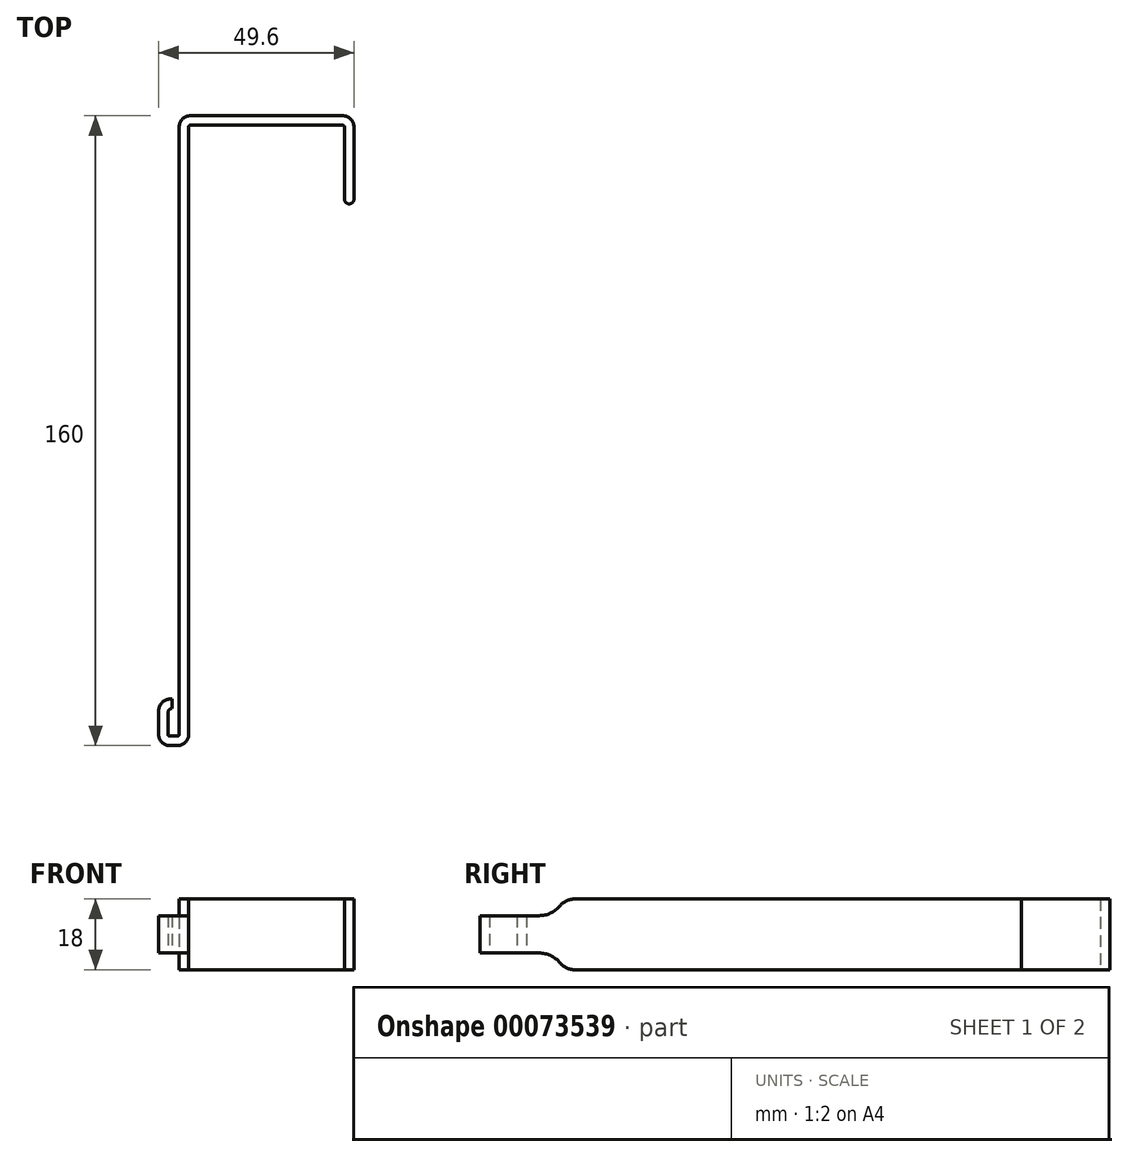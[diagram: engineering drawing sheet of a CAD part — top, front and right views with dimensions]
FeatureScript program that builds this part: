
annotation { "Feature Type Name" : "Feature", "Feature Type Description" : "" }
export const myFeature = defineFeature(function(context is Context, id is Id, definition is map)
    precondition{}
    {
        {
            var Q0;
            Q0=qCreatedBy(makeId("Top.planeOp"),FACE);
            var sketch = newSketch(context, id + "F0", { "sketchPlane" : qUnion([Q0])});
            skLineSegment(sketch, "E0", {"start": v(44.4, -21.2) * mm, "end": v(44.4, -2.9) * mm});
            skLineSegment(sketch, "E1", {"start": v(41.5, 0) * mm, "end": v(2.9, 0) * mm});
            skLineSegment(sketch, "E2", {"start": v(0, -2.9) * mm, "end": v(0, -157.3) * mm});
            skLineSegment(sketch, "E3", {"start": v(2.4, -157.3) * mm, "end": v(2.4, -2.9) * mm});
            skLineSegment(sketch, "E4", {"start": v(2.9, -2.4) * mm, "end": v(41.5, -2.4) * mm});
            skLineSegment(sketch, "E5", {"start": v(42, -2.9) * mm, "end": v(42, -21.2) * mm});
            skArc(sketch, "E6", {"start": v(42, -21.2) * mm, "mid": v(43.2, -22.4) * mm, "end": v(44.4, -21.2) * mm});
            skPoint(sketch, "E7.visualSharp", {"position": v(2.4, -2.4) * mm});
            skArc(sketch, "E7.filletArc", {"start": v(2.9, -2.4) * mm, "mid": v(2.55, -2.55) * mm, "end": v(2.4, -2.9) * mm});
            skPoint(sketch, "E8.visualSharp", {"position": v(42, -2.4) * mm});
            skArc(sketch, "E8.filletArc", {"start": v(42, -2.9) * mm, "mid": v(41.85, -2.55) * mm, "end": v(41.5, -2.4) * mm});
            skPoint(sketch, "E9.visualSharp", {"position": v(44.4, 0) * mm});
            skArc(sketch, "E9.filletArc", {"start": v(44.4, -2.9) * mm, "mid": v(43.55, -0.85) * mm, "end": v(41.5, 0) * mm});
            skPoint(sketch, "E10.visualSharp", {"position": v(0, 0) * mm});
            skArc(sketch, "E10.filletArc", {"start": v(2.9, 0) * mm, "mid": v(0.85, -0.85) * mm, "end": v(0, -2.9) * mm});
            skLineSegment(sketch, "E11", {"start": v(-0.3, -160) * mm, "end": v(-2.5, -160) * mm});
            skLineSegment(sketch, "E12", {"start": v(-5.2, -157.3) * mm, "end": v(-5.2, -151.2) * mm});
            skLineSegment(sketch, "E13", {"start": v(-2.2, -148.2) * mm, "end": v(-1.8, -148.2) * mm});
            skLineSegment(sketch, "E14", {"start": v(-1.8, -148.2) * mm, "end": v(-1.8, -150.6) * mm});
            skLineSegment(sketch, "E15", {"start": v(-2.8, -151.6) * mm, "end": v(-2.8, -157.3) * mm});
            skLineSegment(sketch, "E16", {"start": v(-2.5, -157.6) * mm, "end": v(-0.3, -157.6) * mm});
            skPoint(sketch, "E17.visualSharp", {"position": v(-2.8, -157.6) * mm});
            skArc(sketch, "E17.filletArc", {"start": v(-2.8, -157.3) * mm, "mid": v(-2.71, -157.51) * mm, "end": v(-2.5, -157.6) * mm});
            skPoint(sketch, "E18.visualSharp", {"position": v(0, -157.6) * mm});
            skArc(sketch, "E18.filletArc", {"start": v(-0.3, -157.6) * mm, "mid": v(-0.09, -157.51) * mm, "end": v(0, -157.3) * mm});
            skPoint(sketch, "E19.visualSharp", {"position": v(2.4, -160) * mm});
            skArc(sketch, "E19.filletArc", {"start": v(-0.3, -160) * mm, "mid": v(1.6, -159.2) * mm, "end": v(2.4, -157.3) * mm});
            skPoint(sketch, "E20.visualSharp", {"position": v(-5.2, -160) * mm});
            skArc(sketch, "E20.filletArc", {"start": v(-5.2, -157.3) * mm, "mid": v(-4.4, -159.2) * mm, "end": v(-2.5, -160) * mm});
            skArc(sketch, "E21.filletArc", {"start": v(-1.8, -150.6) * mm, "mid": v(-2.5, -150.9) * mm, "end": v(-2.8, -151.6) * mm});
            skArc(sketch, "E22.filletArc", {"start": v(-2.2, -148.2) * mm, "mid": v(-4.32, -149.08) * mm, "end": v(-5.2, -151.2) * mm});
            skSolve(sketch);
        }
        {
            var Q0;
            Q0=makeQuery(id+"F0.imprint","IMPRINT",FACE,{"disambiguationData":[TD([[makeQuery(id+"F0.imprint","IMPRINT",EDGE,{"derivedFrom":sQuery(id+"F0.wireOp",EDGE,"E0")}),1.0]])]});
            extrude(context, id + "F1", {"entities" : qUnion([Q0]), "depth" : 18 * mm, "symmetric" : true});
        }
        {
            var Q0;
            Q0=qCreatedBy(makeId("Right.planeOp"),FACE);
            var sketch = newSketch(context, id + "F2", { "sketchPlane" : qUnion([Q0])});
            skArc(sketch, "E23", {"start": v(-145, 4.75) * mm, "mid": v(-140.05, 6.8) * mm, "end": v(-138, 11.75) * mm});
            skLineSegment(sketch, "E24", {"start": v(-145, 4.75) * mm, "end": v(-163, 4.75) * mm});
            skLineSegment(sketch, "E25", {"start": v(-163, 4.75) * mm, "end": v(-163, -4.75) * mm});
            skLineSegment(sketch, "E26", {"start": v(-163, -4.75) * mm, "end": v(-145, -4.75) * mm});
            skArc(sketch, "E27", {"start": v(-138, -11.75) * mm, "mid": v(-140.05, -6.8) * mm, "end": v(-145, -4.75) * mm});
            skLineSegment(sketch, "E28", {"start": v(-138, 11.75) * mm, "end": v(-168, 11.75) * mm});
            skLineSegment(sketch, "E29", {"start": v(-168, 11.75) * mm, "end": v(-168, -11.75) * mm});
            skLineSegment(sketch, "E30", {"start": v(-168, -11.75) * mm, "end": v(-138, -11.75) * mm});
            skLineSegment(sketch, "E31", {"start": v(-138, 11.75) * mm, "end": v(-138, -11.75) * mm, "construction": true});
            skLineSegment(sketch, "E32", {"start": v(-168, 0) * mm, "end": v(-138, 0) * mm, "construction": true});
            skSolve(sketch);
        }
        {
            var Q0;
            Q0 = qSketchRegion(id + "F2", true);
            extrude(context, id + "F3", {"entities" : qUnion([Q0]), "operationType" : NewBodyOperationType.REMOVE, "oppositeDirection" : true, "depth" : 20 * mm, "symmetric" : true});
        }
        {
            var Q0;
            Q0=makeQuery(id+"F3.boolean.opBoolean","INTERSECT",EDGE,{"derivedFrom":[makeQuery(id+"F1.opExtrude","CAP_FACE",FACE,{"disambiguationData":[OSD([sQuery(id+"F0.wireOp",EDGE,"E0"),sQuery(id+"F0.wireOp",EDGE,"E1"),sQuery(id+"F0.wireOp",EDGE,"E2"),sQuery(id+"F0.wireOp",EDGE,"E3"),sQuery(id+"F0.wireOp",EDGE,"E4"),sQuery(id+"F0.wireOp",EDGE,"E5"),sQuery(id+"F0.wireOp",EDGE,"E6"),sQuery(id+"F0.wireOp",EDGE,"E7.filletArc"),sQuery(id+"F0.wireOp",EDGE,"E8.filletArc"),sQuery(id+"F0.wireOp",EDGE,"E9.filletArc"),sQuery(id+"F0.wireOp",EDGE,"E10.filletArc"),sQuery(id+"F0.wireOp",EDGE,"E11"),sQuery(id+"F0.wireOp",EDGE,"E12"),sQuery(id+"F0.wireOp",EDGE,"E13"),sQuery(id+"F0.wireOp",EDGE,"E14"),sQuery(id+"F0.wireOp",EDGE,"nkrVinY4-nkwD-jMJN-ugWl-d6SNTpkABNgY"),sQuery(id+"F0.wireOp",EDGE,"E15"),sQuery(id+"F0.wireOp",EDGE,"E16"),sQuery(id+"F0.wireOp",EDGE,"E17.filletArc"),sQuery(id+"F0.wireOp",EDGE,"E18.filletArc"),sQuery(id+"F0.wireOp",EDGE,"E19.filletArc"),sQuery(id+"F0.wireOp",EDGE,"E20.filletArc"),sQuery(id+"F0.wireOp",EDGE,"E21.filletArc"),sQuery(id+"F0.wireOp",EDGE,"E22.filletArc")])],"isStart":false}),makeQuery(id+"F3.opExtrude","SWEPT_FACE",FACE,{"disambiguationData":[OSD([sQuery(id+"F2.wireOp",EDGE,"E23")])]})]});
            var Q1;
            Q1=makeQuery(id+"F3.boolean.opBoolean","INTERSECT",EDGE,{"derivedFrom":[makeQuery(id+"F1.opExtrude","CAP_FACE",FACE,{"disambiguationData":[OSD([sQuery(id+"F0.wireOp",EDGE,"E0"),sQuery(id+"F0.wireOp",EDGE,"E1"),sQuery(id+"F0.wireOp",EDGE,"E2"),sQuery(id+"F0.wireOp",EDGE,"E3"),sQuery(id+"F0.wireOp",EDGE,"E4"),sQuery(id+"F0.wireOp",EDGE,"E5"),sQuery(id+"F0.wireOp",EDGE,"E6"),sQuery(id+"F0.wireOp",EDGE,"E7.filletArc"),sQuery(id+"F0.wireOp",EDGE,"E8.filletArc"),sQuery(id+"F0.wireOp",EDGE,"E9.filletArc"),sQuery(id+"F0.wireOp",EDGE,"E10.filletArc"),sQuery(id+"F0.wireOp",EDGE,"E11"),sQuery(id+"F0.wireOp",EDGE,"E12"),sQuery(id+"F0.wireOp",EDGE,"E13"),sQuery(id+"F0.wireOp",EDGE,"E14"),sQuery(id+"F0.wireOp",EDGE,"nkrVinY4-nkwD-jMJN-ugWl-d6SNTpkABNgY"),sQuery(id+"F0.wireOp",EDGE,"E15"),sQuery(id+"F0.wireOp",EDGE,"E16"),sQuery(id+"F0.wireOp",EDGE,"E17.filletArc"),sQuery(id+"F0.wireOp",EDGE,"E18.filletArc"),sQuery(id+"F0.wireOp",EDGE,"E19.filletArc"),sQuery(id+"F0.wireOp",EDGE,"E20.filletArc"),sQuery(id+"F0.wireOp",EDGE,"E21.filletArc"),sQuery(id+"F0.wireOp",EDGE,"E22.filletArc")])],"isStart":true}),makeQuery(id+"F3.opExtrude","SWEPT_FACE",FACE,{"disambiguationData":[OSD([sQuery(id+"F2.wireOp",EDGE,"E27")])]})]});
            fillet(context, id + "F4", {"entities" : qUnion([Q0, Q1]), "radius" : 5 * mm, "tangentPropagation" : true, "allowEdgeOverflow" : false});
        }
    });
